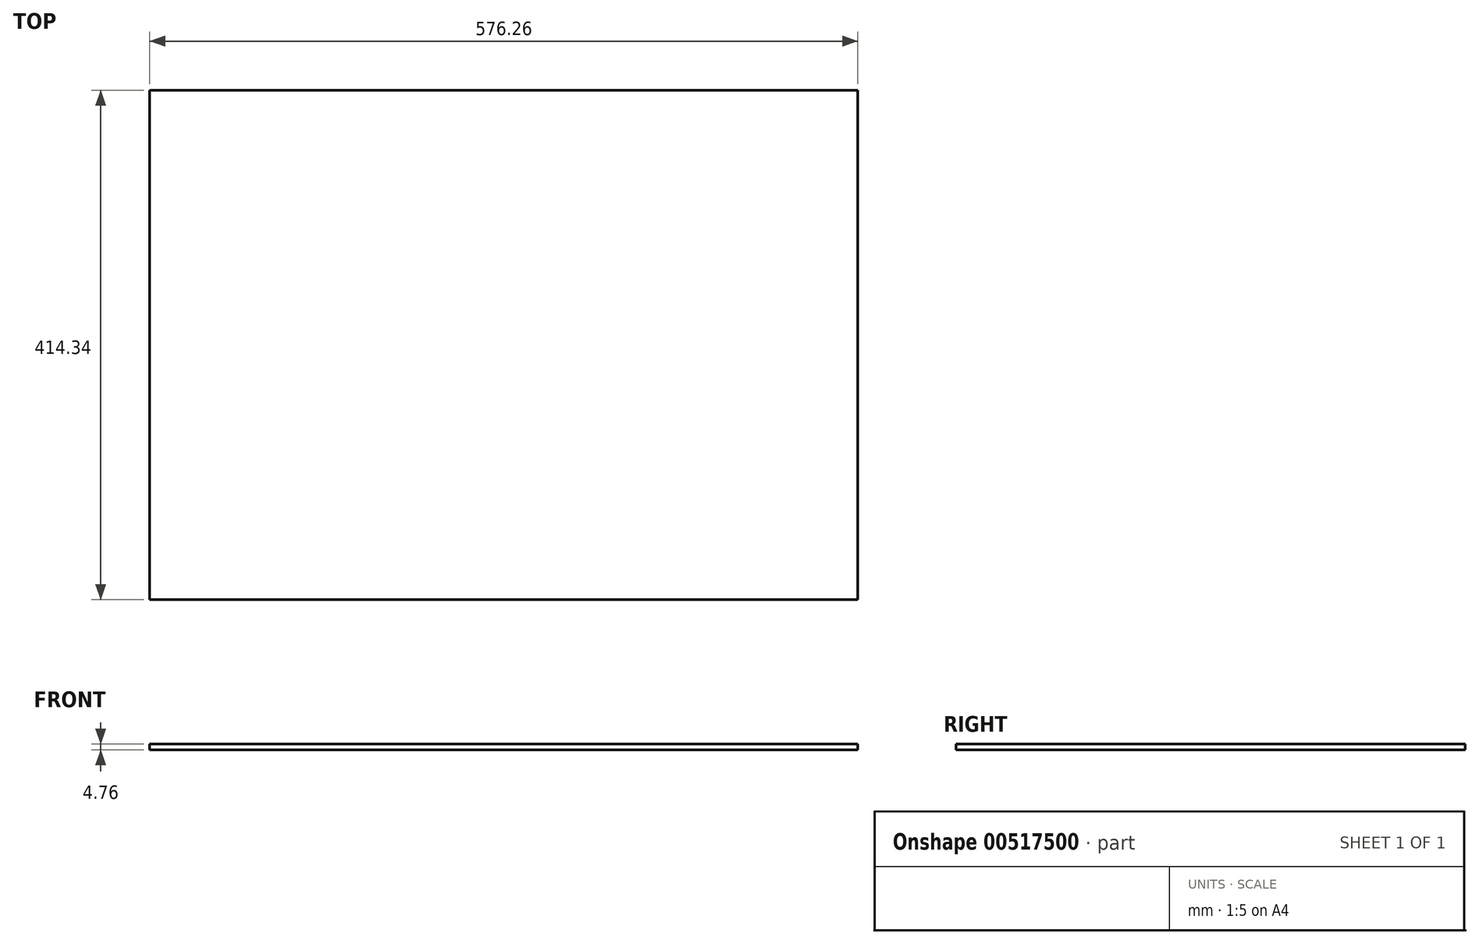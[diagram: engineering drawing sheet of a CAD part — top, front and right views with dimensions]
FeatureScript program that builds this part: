
annotation { "Feature Type Name" : "Feature", "Feature Type Description" : "" }
export const myFeature = defineFeature(function(context is Context, id is Id, definition is map)
    precondition{}
    {
        {
            var Q0;
            Q0=qCreatedBy(makeId("Top.planeOp"),FACE);
            var sketch = newSketch(context, id + "F0", { "sketchPlane" : qUnion([Q0])});
            skLineSegment(sketch, "E0.bottom", {"start": v(-288.13, 207.17) * mm, "end": v(288.13, 207.17) * mm});
            skLineSegment(sketch, "E0.top", {"start": v(-288.13, -207.17) * mm, "end": v(288.13, -207.17) * mm});
            skLineSegment(sketch, "E0.left", {"start": v(-288.13, 207.17) * mm, "end": v(-288.13, -207.17) * mm});
            skLineSegment(sketch, "E0.right", {"start": v(288.13, 207.17) * mm, "end": v(288.13, -207.17) * mm});
            skPoint(sketch, "E0.middle", {"position": v(0, 0) * mm});
            skSolve(sketch);
        }
        {
            var Q0;
            Q0 = qSketchRegion(id + "F0", true);
            extrude(context, id + "F1", {"entities" : qUnion([Q0]), "depth" : 4.76 * mm, "offsetDistance" : 25.4 * mm});
        }
    });
